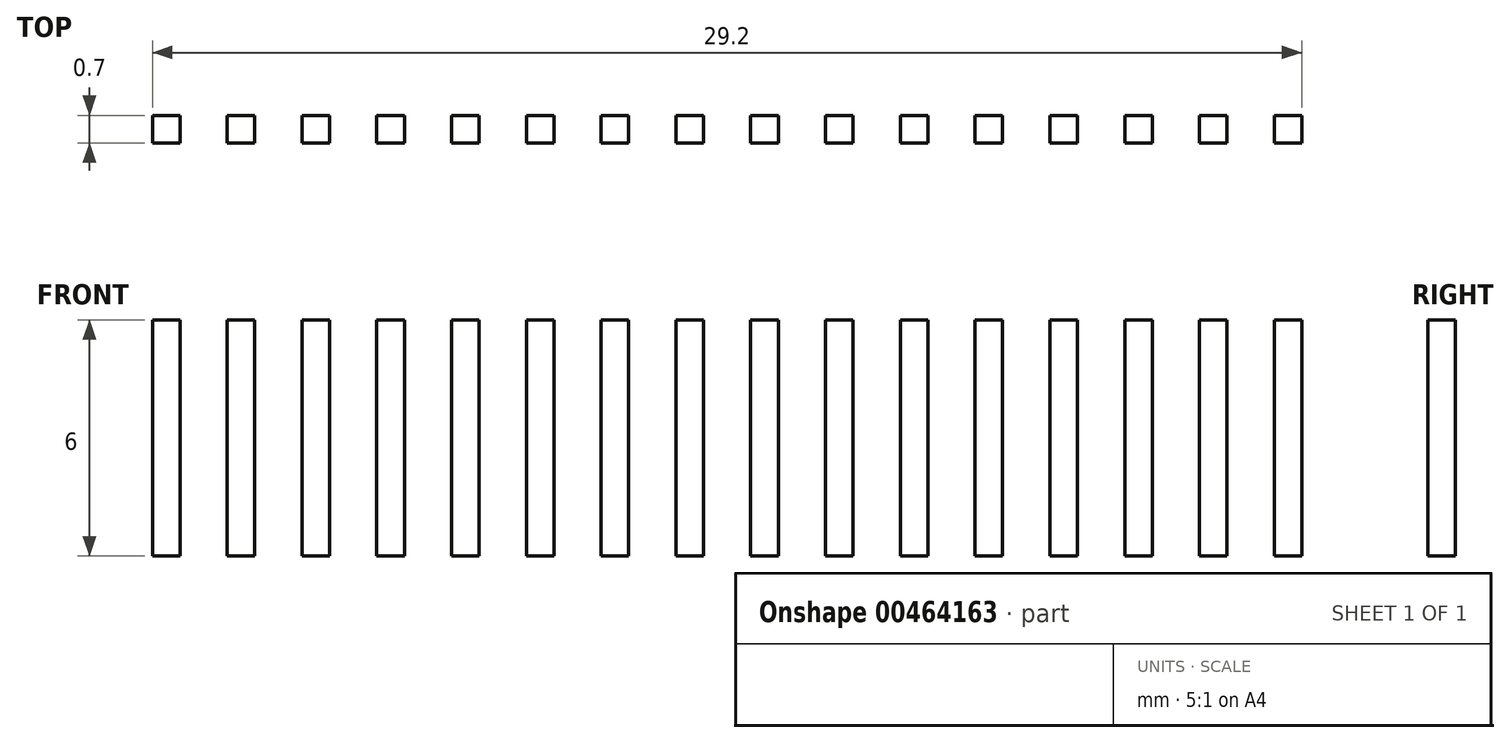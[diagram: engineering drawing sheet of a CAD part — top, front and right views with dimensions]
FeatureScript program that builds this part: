
annotation { "Feature Type Name" : "Feature", "Feature Type Description" : "" }
export const myFeature = defineFeature(function(context is Context, id is Id, definition is map)
    precondition{}
    {
        {
            var Q0;
            Q0=qCreatedBy(makeId("Top.planeOp"),FACE);
            var sketch = newSketch(context, id + "F0", { "sketchPlane" : qUnion([Q0])});
            skLineSegment(sketch, "E0.bottom", {"start": v(0, 0) * mm, "end": v(0.7, 0) * mm});
            skLineSegment(sketch, "E0.top", {"start": v(0, -0.7) * mm, "end": v(0.7, -0.7) * mm});
            skLineSegment(sketch, "E0.left", {"start": v(0, 0) * mm, "end": v(0, -0.7) * mm});
            skLineSegment(sketch, "E0.right", {"start": v(0.7, 0) * mm, "end": v(0.7, -0.7) * mm});
            skLineSegment(sketch, "E1.1.0.0", {"start": v(1.9, 0) * mm, "end": v(1.9, -0.7) * mm});
            skLineSegment(sketch, "E1.1.0.1", {"start": v(2.6, 0) * mm, "end": v(2.6, -0.7) * mm});
            skLineSegment(sketch, "E1.1.0.2", {"start": v(1.9, -0.7) * mm, "end": v(2.6, -0.7) * mm});
            skLineSegment(sketch, "E1.1.0.3", {"start": v(1.9, 0) * mm, "end": v(2.6, 0) * mm});
            skLineSegment(sketch, "E1.2.0.0", {"start": v(3.8, 0) * mm, "end": v(3.8, -0.7) * mm});
            skLineSegment(sketch, "E1.2.0.1", {"start": v(4.5, 0) * mm, "end": v(4.5, -0.7) * mm});
            skLineSegment(sketch, "E1.2.0.2", {"start": v(3.8, -0.7) * mm, "end": v(4.5, -0.7) * mm});
            skLineSegment(sketch, "E1.2.0.3", {"start": v(3.8, 0) * mm, "end": v(4.5, 0) * mm});
            skLineSegment(sketch, "E1.3.0.0", {"start": v(5.7, 0) * mm, "end": v(5.7, -0.7) * mm});
            skLineSegment(sketch, "E1.3.0.1", {"start": v(6.4, 0) * mm, "end": v(6.4, -0.7) * mm});
            skLineSegment(sketch, "E1.3.0.2", {"start": v(5.7, -0.7) * mm, "end": v(6.4, -0.7) * mm});
            skLineSegment(sketch, "E1.3.0.3", {"start": v(5.7, 0) * mm, "end": v(6.4, 0) * mm});
            skLineSegment(sketch, "E1.4.0.0", {"start": v(7.6, 0) * mm, "end": v(7.6, -0.7) * mm});
            skLineSegment(sketch, "E1.4.0.1", {"start": v(8.3, 0) * mm, "end": v(8.3, -0.7) * mm});
            skLineSegment(sketch, "E1.4.0.2", {"start": v(7.6, -0.7) * mm, "end": v(8.3, -0.7) * mm});
            skLineSegment(sketch, "E1.4.0.3", {"start": v(7.6, 0) * mm, "end": v(8.3, 0) * mm});
            skLineSegment(sketch, "E1.5.0.0", {"start": v(9.5, 0) * mm, "end": v(9.5, -0.7) * mm});
            skLineSegment(sketch, "E1.5.0.1", {"start": v(10.2, 0) * mm, "end": v(10.2, -0.7) * mm});
            skLineSegment(sketch, "E1.5.0.2", {"start": v(9.5, -0.7) * mm, "end": v(10.2, -0.7) * mm});
            skLineSegment(sketch, "E1.5.0.3", {"start": v(9.5, 0) * mm, "end": v(10.2, 0) * mm});
            skLineSegment(sketch, "E1.6.0.0", {"start": v(11.4, 0) * mm, "end": v(11.4, -0.7) * mm});
            skLineSegment(sketch, "E1.6.0.1", {"start": v(12.1, 0) * mm, "end": v(12.1, -0.7) * mm});
            skLineSegment(sketch, "E1.6.0.2", {"start": v(11.4, -0.7) * mm, "end": v(12.1, -0.7) * mm});
            skLineSegment(sketch, "E1.6.0.3", {"start": v(11.4, 0) * mm, "end": v(12.1, 0) * mm});
            skLineSegment(sketch, "E1.7.0.0", {"start": v(13.3, 0) * mm, "end": v(13.3, -0.7) * mm});
            skLineSegment(sketch, "E1.7.0.1", {"start": v(14, 0) * mm, "end": v(14, -0.7) * mm});
            skLineSegment(sketch, "E1.7.0.2", {"start": v(13.3, -0.7) * mm, "end": v(14, -0.7) * mm});
            skLineSegment(sketch, "E1.7.0.3", {"start": v(13.3, 0) * mm, "end": v(14, 0) * mm});
            skLineSegment(sketch, "E1.8.0.0", {"start": v(15.2, 0) * mm, "end": v(15.2, -0.7) * mm});
            skLineSegment(sketch, "E1.8.0.1", {"start": v(15.9, 0) * mm, "end": v(15.9, -0.7) * mm});
            skLineSegment(sketch, "E1.8.0.2", {"start": v(15.2, -0.7) * mm, "end": v(15.9, -0.7) * mm});
            skLineSegment(sketch, "E1.8.0.3", {"start": v(15.2, 0) * mm, "end": v(15.9, 0) * mm});
            skLineSegment(sketch, "E1.9.0.0", {"start": v(17.1, 0) * mm, "end": v(17.1, -0.7) * mm});
            skLineSegment(sketch, "E1.9.0.1", {"start": v(17.8, 0) * mm, "end": v(17.8, -0.7) * mm});
            skLineSegment(sketch, "E1.9.0.2", {"start": v(17.1, -0.7) * mm, "end": v(17.8, -0.7) * mm});
            skLineSegment(sketch, "E1.9.0.3", {"start": v(17.1, 0) * mm, "end": v(17.8, 0) * mm});
            skLineSegment(sketch, "E1.10.0.0", {"start": v(19, 0) * mm, "end": v(19, -0.7) * mm});
            skLineSegment(sketch, "E1.10.0.1", {"start": v(19.7, 0) * mm, "end": v(19.7, -0.7) * mm});
            skLineSegment(sketch, "E1.10.0.2", {"start": v(19, -0.7) * mm, "end": v(19.7, -0.7) * mm});
            skLineSegment(sketch, "E1.10.0.3", {"start": v(19, 0) * mm, "end": v(19.7, 0) * mm});
            skLineSegment(sketch, "E1.11.0.0", {"start": v(20.9, 0) * mm, "end": v(20.9, -0.7) * mm});
            skLineSegment(sketch, "E1.11.0.1", {"start": v(21.6, 0) * mm, "end": v(21.6, -0.7) * mm});
            skLineSegment(sketch, "E1.11.0.2", {"start": v(20.9, -0.7) * mm, "end": v(21.6, -0.7) * mm});
            skLineSegment(sketch, "E1.11.0.3", {"start": v(20.9, 0) * mm, "end": v(21.6, 0) * mm});
            skLineSegment(sketch, "E1.12.0.0", {"start": v(22.8, 0) * mm, "end": v(22.8, -0.7) * mm});
            skLineSegment(sketch, "E1.12.0.1", {"start": v(23.5, 0) * mm, "end": v(23.5, -0.7) * mm});
            skLineSegment(sketch, "E1.12.0.2", {"start": v(22.8, -0.7) * mm, "end": v(23.5, -0.7) * mm});
            skLineSegment(sketch, "E1.12.0.3", {"start": v(22.8, 0) * mm, "end": v(23.5, 0) * mm});
            skLineSegment(sketch, "E1.13.0.0", {"start": v(24.7, 0) * mm, "end": v(24.7, -0.7) * mm});
            skLineSegment(sketch, "E1.13.0.1", {"start": v(25.4, 0) * mm, "end": v(25.4, -0.7) * mm});
            skLineSegment(sketch, "E1.13.0.2", {"start": v(24.7, -0.7) * mm, "end": v(25.4, -0.7) * mm});
            skLineSegment(sketch, "E1.13.0.3", {"start": v(24.7, 0) * mm, "end": v(25.4, 0) * mm});
            skLineSegment(sketch, "E1.14.0.0", {"start": v(26.6, 0) * mm, "end": v(26.6, -0.7) * mm});
            skLineSegment(sketch, "E1.14.0.1", {"start": v(27.3, 0) * mm, "end": v(27.3, -0.7) * mm});
            skLineSegment(sketch, "E1.14.0.2", {"start": v(26.6, -0.7) * mm, "end": v(27.3, -0.7) * mm});
            skLineSegment(sketch, "E1.14.0.3", {"start": v(26.6, 0) * mm, "end": v(27.3, 0) * mm});
            skLineSegment(sketch, "E1.15.0.0", {"start": v(28.5, 0) * mm, "end": v(28.5, -0.7) * mm});
            skLineSegment(sketch, "E1.15.0.1", {"start": v(29.2, 0) * mm, "end": v(29.2, -0.7) * mm});
            skLineSegment(sketch, "E1.15.0.2", {"start": v(28.5, -0.7) * mm, "end": v(29.2, -0.7) * mm});
            skLineSegment(sketch, "E1.15.0.3", {"start": v(28.5, 0) * mm, "end": v(29.2, 0) * mm});
            skLineSegment(sketch, "E1.direction1", {"start": v(0, -0.7) * mm, "end": v(1.9, -0.7) * mm, "construction": true});
            skSolve(sketch);
        }
        {
            var Q0;
            Q0 = qSketchRegion(id + "F0", true);
            extrude(context, id + "F1", {"entities" : qUnion([Q0]), "depth" : 6 * mm});
        }
    });
